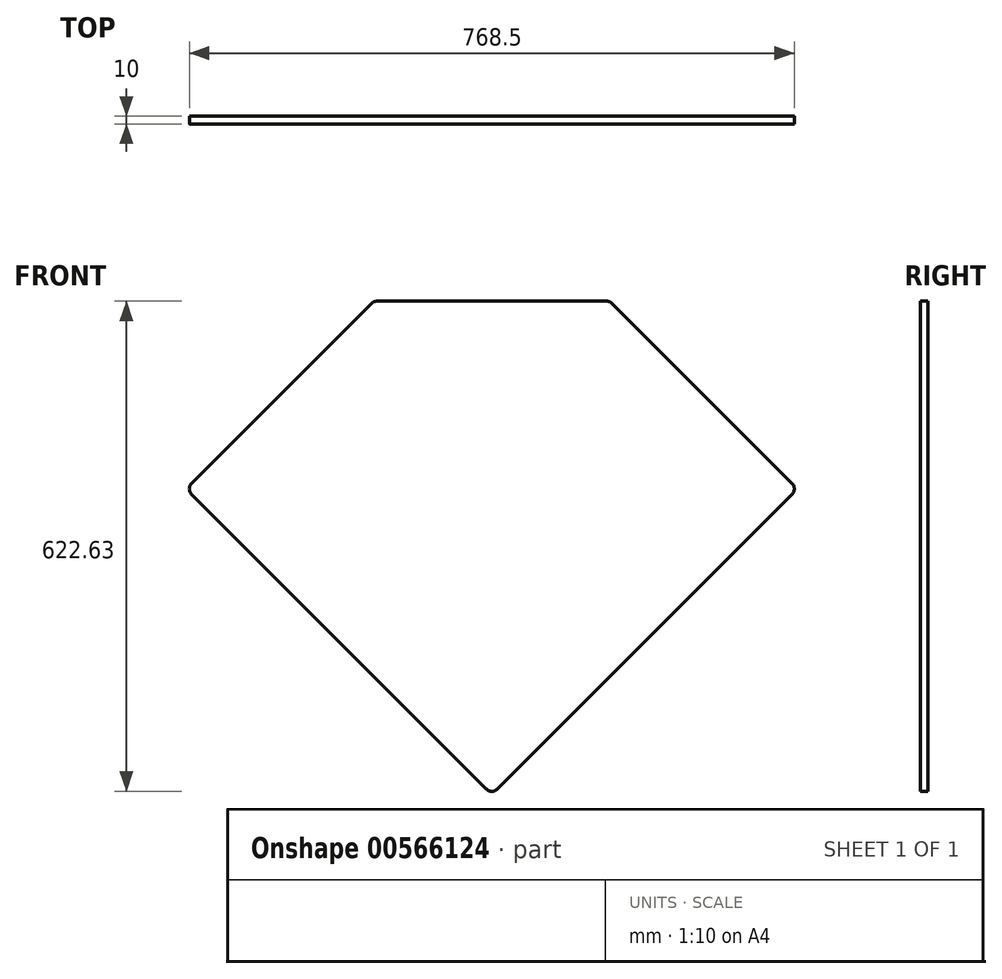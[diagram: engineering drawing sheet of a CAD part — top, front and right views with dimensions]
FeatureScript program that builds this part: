
annotation { "Feature Type Name" : "Feature", "Feature Type Description" : "" }
export const myFeature = defineFeature(function(context is Context, id is Id, definition is map)
    precondition{}
    {
        {
            var Q0;
            Q0=qCreatedBy(makeId("Front.planeOp"),FACE);
            var sketch = newSketch(context, id + "F0", { "sketchPlane" : qUnion([Q0])});
            skLineSegment(sketch, "E0", {"start": v(-300, 0) * mm, "end": v(-152.93, 147.07) * mm});
            skLineSegment(sketch, "E1", {"start": v(152.93, 147.07) * mm, "end": v(300, 0) * mm});
            skPoint(sketch, "E2.endSnap0", {"position": v(150, 150) * mm});
            skPoint(sketch, "E3.orphan", {"position": v(0, 300) * mm});
            skLineSegment(sketch, "E4", {"start": v(-145.86, 150) * mm, "end": v(145.86, 150) * mm});
            skLineSegment(sketch, "E5", {"start": v(-300, 0) * mm, "end": v(-381.32, -81.32) * mm});
            skLineSegment(sketch, "E6", {"start": v(-381.32, -95.46) * mm, "end": v(-155.04, -321.73) * mm});
            skLineSegment(sketch, "E7", {"start": v(300, 0) * mm, "end": v(381.32, -81.32) * mm});
            skLineSegment(sketch, "E8", {"start": v(381.32, -95.46) * mm, "end": v(155.04, -321.73) * mm});
            skPoint(sketch, "E9.visualSharp", {"position": v(-388.39, -88.39) * mm});
            skArc(sketch, "E9.filletArc", {"start": v(-381.32, -81.32) * mm, "mid": v(-384.25, -88.39) * mm, "end": v(-381.32, -95.46) * mm});
            skPoint(sketch, "E10.visualSharp", {"position": v(147.97, -328.8) * mm});
            skPoint(sketch, "E11.visualSharp", {"position": v(388.39, -88.39) * mm});
            skArc(sketch, "E11.filletArc", {"start": v(381.32, -95.46) * mm, "mid": v(384.25, -88.39) * mm, "end": v(381.32, -81.32) * mm});
            skPoint(sketch, "E12.visualSharp", {"position": v(-150, 150) * mm});
            skArc(sketch, "E12.filletArc", {"start": v(-145.86, 150) * mm, "mid": v(-149.68, 149.24) * mm, "end": v(-152.93, 147.07) * mm});
            skArc(sketch, "E13.filletArc", {"start": v(152.93, 147.07) * mm, "mid": v(149.68, 149.24) * mm, "end": v(145.86, 150) * mm});
            skLineSegment(sketch, "E14", {"start": v(-155.04, -321.73) * mm, "end": v(-7.07, -469.7) * mm});
            skLineSegment(sketch, "E15", {"start": v(7.07, -469.7) * mm, "end": v(155.04, -321.73) * mm});
            skPoint(sketch, "E16.visualSharp", {"position": v(0, -476.78) * mm});
            skArc(sketch, "E16.filletArc", {"start": v(-7.07, -469.7) * mm, "mid": v(0, -472.63) * mm, "end": v(7.07, -469.7) * mm});
            skSolve(sketch);
        }
        {
            var Q0;
            Q0=qSketchRegion(id+"F0",true);
            var Q1;
            {var subQ0=sQuery(id+"F0.wireOp",EDGE,"f3315127-8726-48a4-a6a5-5769ba37091d.0");Q1=makeQuery(id+"F0.imprint","IMPRINT",FACE,{"disambiguationData":[TD([[makeQuery(id+"F0.imprint","IMPRINT",EDGE,{"derivedFrom":subQ0}),-1.0]])]});}
            var Q2;
            {var subQ0=sQuery(id+"F0.wireOp",EDGE,"dds854Fr-lJqI-Rvvb-gUDD-RAXXg9cEFkbB");Q2=makeQuery(id+"F0.imprint","IMPRINT",FACE,{"disambiguationData":[TD([[makeQuery(id+"F0.imprint","IMPRINT",EDGE,{"derivedFrom":subQ0}),-1.0]])]});}
            extrude(context, id + "F1", {"entities" : qUnion([Q0, Q1, Q2]), "depth" : 10 * mm, "offsetDistance" : 25 * mm});
        }
    });
